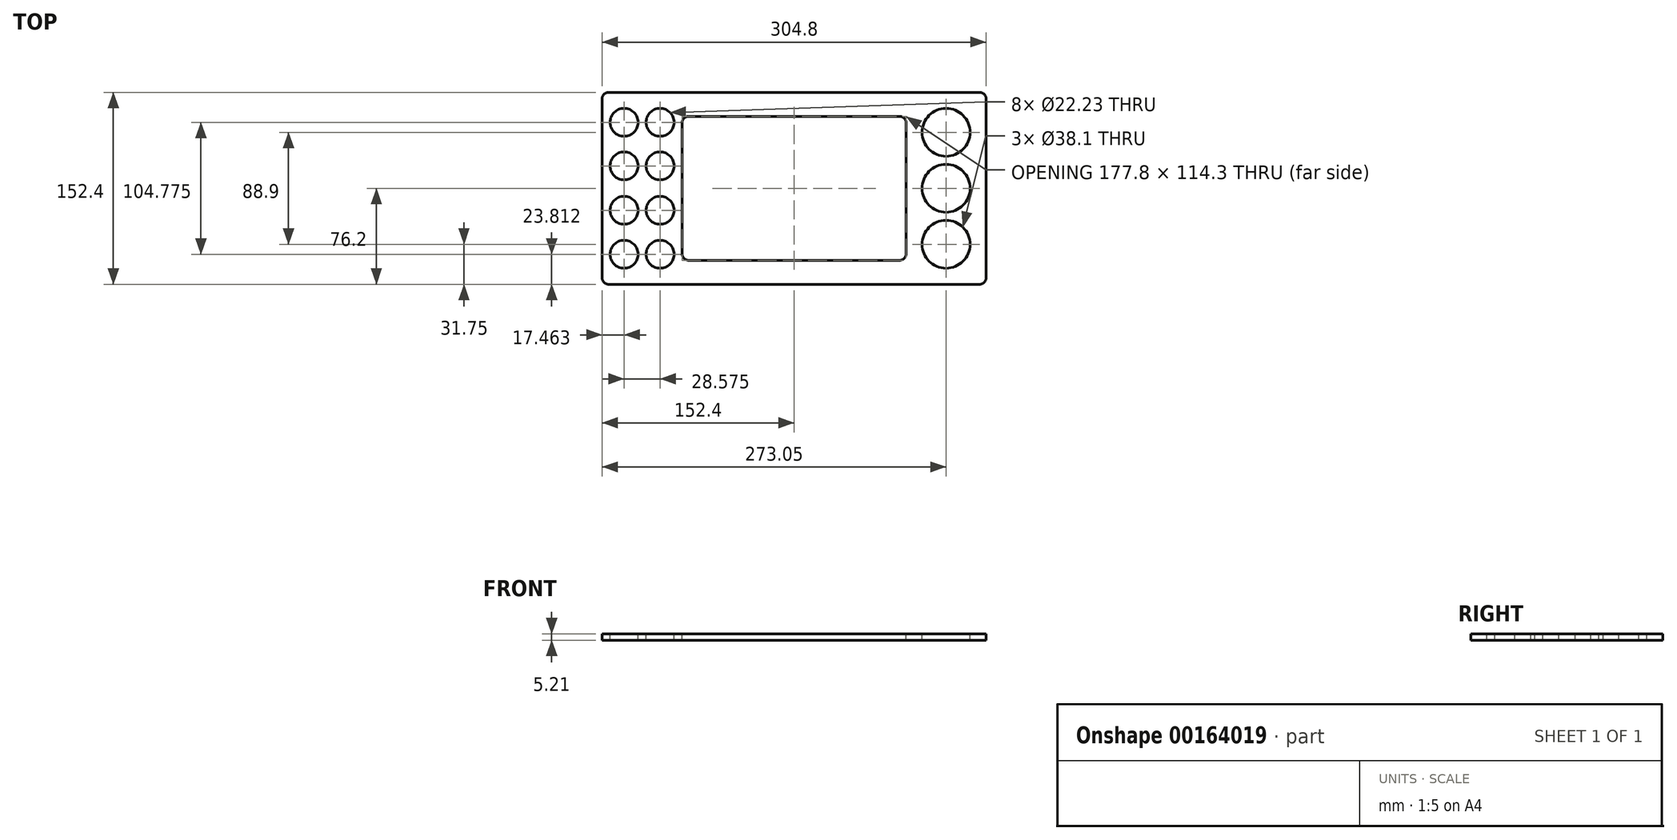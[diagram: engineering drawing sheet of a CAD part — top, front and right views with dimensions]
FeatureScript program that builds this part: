
annotation { "Feature Type Name" : "Feature", "Feature Type Description" : "" }
export const myFeature = defineFeature(function(context is Context, id is Id, definition is map)
    precondition{}
    {
        {
            var Q0;
            Q0=qCreatedBy(makeId("Top.planeOp"),FACE);
            var sketch = newSketch(context, id + "F0", { "sketchPlane" : qUnion([Q0])});
            skLineSegment(sketch, "E0.bottom", {"start": v(152.4, -76.2) * mm, "end": v(-152.4, -76.2) * mm});
            skLineSegment(sketch, "E0.top", {"start": v(152.4, 76.2) * mm, "end": v(-152.4, 76.2) * mm});
            skLineSegment(sketch, "E0.left", {"start": v(152.4, -76.2) * mm, "end": v(152.4, 76.2) * mm});
            skLineSegment(sketch, "E0.right", {"start": v(-152.4, -76.2) * mm, "end": v(-152.4, 76.2) * mm});
            skPoint(sketch, "E0.middle", {"position": v(0, 0) * mm});
            skSolve(sketch);
        }
        {
            var Q0;
            Q0 = qSketchRegion(id + "F0", true);
            extrude(context, id + "F1", {"entities" : qUnion([Q0]), "depth" : 5.2 * mm});
        }
        {
            var Q0;
            Q0=makeQuery(id+"F1.opExtrude","CAP_FACE",FACE,{"disambiguationData":[OSD([sQuery(id+"F0.wireOp",EDGE,"E0.bottom"),sQuery(id+"F0.wireOp",EDGE,"E0.top"),sQuery(id+"F0.wireOp",EDGE,"E0.left"),sQuery(id+"F0.wireOp",EDGE,"E0.right")])],"isStart":false});
            var sketch = newSketch(context, id + "F2", { "sketchPlane" : qUnion([Q0])});
            skLineSegment(sketch, "E1.bottom", {"start": v(88.9, -57.15) * mm, "end": v(-88.9, -57.15) * mm});
            skLineSegment(sketch, "E1.top", {"start": v(88.9, 57.15) * mm, "end": v(-88.9, 57.15) * mm});
            skLineSegment(sketch, "E1.left", {"start": v(88.9, -57.15) * mm, "end": v(88.9, 57.15) * mm});
            skLineSegment(sketch, "E1.right", {"start": v(-88.9, -57.15) * mm, "end": v(-88.9, 57.15) * mm});
            skPoint(sketch, "E1.middle", {"position": v(0, 0) * mm});
            skSolve(sketch);
        }
        {
            var Q0;
            Q0=makeQuery(id+"F2.imprint","IMPRINT",FACE,{"disambiguationData":[TD([[makeQuery(id+"F2.imprint","IMPRINT",EDGE,{"derivedFrom":sQuery(id+"F2.wireOp",EDGE,"E1.bottom")}),-1.0]])]});
            extrude(context, id + "F3", {"entities" : qUnion([Q0]), "operationType" : NewBodyOperationType.REMOVE, "endBound" : BoundingType.THROUGH_ALL, "oppositeDirection" : true, "depth" : 25.4 * mm});
        }
        {
            var Q0;
            Q0=makeQuery(id+"F1.opExtrude","CAP_FACE",FACE,{"disambiguationData":[OSD([sQuery(id+"F0.wireOp",EDGE,"E0.bottom"),sQuery(id+"F0.wireOp",EDGE,"E0.top"),sQuery(id+"F0.wireOp",EDGE,"E0.left"),sQuery(id+"F0.wireOp",EDGE,"E0.right")])],"isStart":false});
            var sketch = newSketch(context, id + "F4", { "sketchPlane" : qUnion([Q0])});
            skCircle(sketch, "E2", {"center": v(120.65, 44.45) * mm, "radius": 19.05 * mm});
            skCircle(sketch, "E3", {"center": v(120.65, 0) * mm, "radius": 19.05 * mm});
            skCircle(sketch, "E4", {"center": v(120.65, -44.45) * mm, "radius": 19.05 * mm});
            skSolve(sketch);
        }
        {
            var Q0;
            Q0=makeQuery(id+"F4.imprint","IMPRINT",FACE,{"disambiguationData":[TD([[makeQuery(id+"F4.imprint","IMPRINT",EDGE,{"derivedFrom":sQuery(id+"F4.wireOp",EDGE,"E4")}),1.0]])]});
            var Q1;
            Q1=makeQuery(id+"F4.imprint","IMPRINT",FACE,{"disambiguationData":[TD([[makeQuery(id+"F4.imprint","IMPRINT",EDGE,{"derivedFrom":sQuery(id+"F4.wireOp",EDGE,"E3")}),1.0]])]});
            var Q2;
            Q2=makeQuery(id+"F4.imprint","IMPRINT",FACE,{"disambiguationData":[TD([[makeQuery(id+"F4.imprint","IMPRINT",EDGE,{"derivedFrom":sQuery(id+"F4.wireOp",EDGE,"E2")}),1.0]])]});
            extrude(context, id + "F5", {"entities" : qUnion([Q0, Q1, Q2]), "operationType" : NewBodyOperationType.REMOVE, "endBound" : BoundingType.THROUGH_ALL, "oppositeDirection" : true, "depth" : 25.4 * mm});
        }
        {
            var Q0;
            Q0=makeQuery(id+"F1.opExtrude","CAP_FACE",FACE,{"disambiguationData":[OSD([sQuery(id+"F0.wireOp",EDGE,"E0.bottom"),sQuery(id+"F0.wireOp",EDGE,"E0.top"),sQuery(id+"F0.wireOp",EDGE,"E0.left"),sQuery(id+"F0.wireOp",EDGE,"E0.right")])],"isStart":false});
            var sketch = newSketch(context, id + "F6", { "sketchPlane" : qUnion([Q0])});
            skCircle(sketch, "E5", {"center": v(-134.94, 52.39) * mm, "radius": 11.11 * mm});
            skCircle(sketch, "E6", {"center": v(-106.36, 52.39) * mm, "radius": 11.11 * mm});
            skCircle(sketch, "E7", {"center": v(-134.94, -52.39) * mm, "radius": 11.11 * mm});
            skCircle(sketch, "E8", {"center": v(-106.36, -52.39) * mm, "radius": 11.11 * mm});
            skCircle(sketch, "E9", {"center": v(-134.94, -17.46) * mm, "radius": 11.11 * mm});
            skCircle(sketch, "E10", {"center": v(-106.36, -17.46) * mm, "radius": 11.11 * mm});
            skCircle(sketch, "E11", {"center": v(-134.94, 17.8) * mm, "radius": 11.11 * mm});
            skCircle(sketch, "E12", {"center": v(-106.36, 17.8) * mm, "radius": 11.11 * mm});
            skSolve(sketch);
        }
        {
            var Q0;
            Q0=makeQuery(id+"F6.imprint","IMPRINT",FACE,{"disambiguationData":[TD([[makeQuery(id+"F6.imprint","IMPRINT",EDGE,{"derivedFrom":sQuery(id+"F6.wireOp",EDGE,"E5")}),1.0]])]});
            var Q1;
            Q1=makeQuery(id+"F6.imprint","IMPRINT",FACE,{"disambiguationData":[TD([[makeQuery(id+"F6.imprint","IMPRINT",EDGE,{"derivedFrom":sQuery(id+"F6.wireOp",EDGE,"E6")}),1.0]])]});
            var Q2;
            Q2=makeQuery(id+"F6.imprint","IMPRINT",FACE,{"disambiguationData":[TD([[makeQuery(id+"F6.imprint","IMPRINT",EDGE,{"derivedFrom":sQuery(id+"F6.wireOp",EDGE,"E11")}),1.0]])]});
            var Q3;
            Q3=makeQuery(id+"F6.imprint","IMPRINT",FACE,{"disambiguationData":[TD([[makeQuery(id+"F6.imprint","IMPRINT",EDGE,{"derivedFrom":sQuery(id+"F6.wireOp",EDGE,"E12")}),1.0]])]});
            var Q4;
            Q4=makeQuery(id+"F6.imprint","IMPRINT",FACE,{"disambiguationData":[TD([[makeQuery(id+"F6.imprint","IMPRINT",EDGE,{"derivedFrom":sQuery(id+"F6.wireOp",EDGE,"E9")}),1.0]])]});
            var Q5;
            Q5=makeQuery(id+"F6.imprint","IMPRINT",FACE,{"disambiguationData":[TD([[makeQuery(id+"F6.imprint","IMPRINT",EDGE,{"derivedFrom":sQuery(id+"F6.wireOp",EDGE,"E10")}),1.0]])]});
            var Q6;
            Q6=makeQuery(id+"F6.imprint","IMPRINT",FACE,{"disambiguationData":[TD([[makeQuery(id+"F6.imprint","IMPRINT",EDGE,{"derivedFrom":sQuery(id+"F6.wireOp",EDGE,"E7")}),1.0]])]});
            var Q7;
            Q7=makeQuery(id+"F6.imprint","IMPRINT",FACE,{"disambiguationData":[TD([[makeQuery(id+"F6.imprint","IMPRINT",EDGE,{"derivedFrom":sQuery(id+"F6.wireOp",EDGE,"E8")}),1.0]])]});
            extrude(context, id + "F7", {"entities" : qUnion([Q0, Q1, Q2, Q3, Q4, Q5, Q6, Q7]), "operationType" : NewBodyOperationType.REMOVE, "endBound" : BoundingType.THROUGH_ALL, "oppositeDirection" : true, "depth" : 25.4 * mm});
        }
        {
            var Q0;
            Q0=makeQuery(id+"F1.opExtrude","SWEPT_BODY",BODY,{"disambiguationData":[OSD([sQuery(id+"F0.wireOp",EDGE,"E0.bottom"),sQuery(id+"F0.wireOp",EDGE,"E0.top"),sQuery(id+"F0.wireOp",EDGE,"E0.left"),sQuery(id+"F0.wireOp",EDGE,"E0.right")])]});
            transform(context, id + "F8", {"entities" : qUnion([Q0]), "transformType" : TransformType.TRANSLATION_3D, "dx" : 0 * mm, "dy" : 0 * mm, "dz" : 0 * mm, "makeCopy" : true});
        }
        {
            var Q0;
            Q0=makeQuery(id+"F8.opPattern","COPY",BODY,{"derivedFrom":makeQuery(id+"F1.opExtrude","SWEPT_BODY",BODY,{"disambiguationData":[OSD([sQuery(id+"F0.wireOp",EDGE,"E0.bottom"),sQuery(id+"F0.wireOp",EDGE,"E0.top"),sQuery(id+"F0.wireOp",EDGE,"E0.left"),sQuery(id+"F0.wireOp",EDGE,"E0.right")])]}),"instanceName":"1"});
            deleteBodies(context, id + "F9", {"entities" : qUnion([Q0])});
        }
        {
            var Q0;
            Q0=makeQuery(id+"F1.opExtrude","SWEPT_EDGE",EDGE,{"disambiguationData":[OSD([sQuery(id+"F0.wireOp",EDGE,"E0.bottom"),sQuery(id+"F0.wireOp",EDGE,"E0.right")])]});
            var Q1;
            Q1=makeQuery(id+"F1.opExtrude","SWEPT_EDGE",EDGE,{"disambiguationData":[OSD([sQuery(id+"F0.wireOp",EDGE,"E0.top"),sQuery(id+"F0.wireOp",EDGE,"E0.right")])]});
            var Q2;
            Q2=makeQuery(id+"F1.opExtrude","SWEPT_EDGE",EDGE,{"disambiguationData":[OSD([sQuery(id+"F0.wireOp",EDGE,"E0.top"),sQuery(id+"F0.wireOp",EDGE,"E0.left")])]});
            var Q3;
            Q3=makeQuery(id+"F1.opExtrude","SWEPT_EDGE",EDGE,{"disambiguationData":[OSD([sQuery(id+"F0.wireOp",EDGE,"E0.bottom"),sQuery(id+"F0.wireOp",EDGE,"E0.left")])]});
            fillet(context, id + "F10", {"entities" : qUnion([Q0, Q1, Q2, Q3]), "radius" : 5.08 * mm, "tangentPropagation" : true, "allowEdgeOverflow" : false});
        }
        {
            var Q0;
            Q0=makeQuery(id+"F3.boolean.opBoolean","COPY",EDGE,{"derivedFrom":makeQuery(id+"F3.opExtrude","SWEPT_EDGE",EDGE,{"disambiguationData":[OSD([sQuery(id+"F2.wireOp",EDGE,"E1.top"),sQuery(id+"F2.wireOp",EDGE,"E1.right")])]})});
            var Q1;
            Q1=makeQuery(id+"F3.boolean.opBoolean","COPY",EDGE,{"derivedFrom":makeQuery(id+"F3.opExtrude","SWEPT_EDGE",EDGE,{"disambiguationData":[OSD([sQuery(id+"F2.wireOp",EDGE,"E1.bottom"),sQuery(id+"F2.wireOp",EDGE,"E1.right")])]})});
            var Q2;
            Q2=makeQuery(id+"F3.boolean.opBoolean","COPY",EDGE,{"derivedFrom":makeQuery(id+"F3.opExtrude","SWEPT_EDGE",EDGE,{"disambiguationData":[OSD([sQuery(id+"F2.wireOp",EDGE,"E1.top"),sQuery(id+"F2.wireOp",EDGE,"E1.left")])]})});
            var Q3;
            Q3=makeQuery(id+"F3.boolean.opBoolean","COPY",EDGE,{"derivedFrom":makeQuery(id+"F3.opExtrude","SWEPT_EDGE",EDGE,{"disambiguationData":[OSD([sQuery(id+"F2.wireOp",EDGE,"E1.bottom"),sQuery(id+"F2.wireOp",EDGE,"E1.left")])]})});
            fillet(context, id + "F11", {"entities" : qUnion([Q0, Q1, Q2, Q3]), "radius" : 5.08 * mm, "tangentPropagation" : true, "allowEdgeOverflow" : false});
        }
    });
